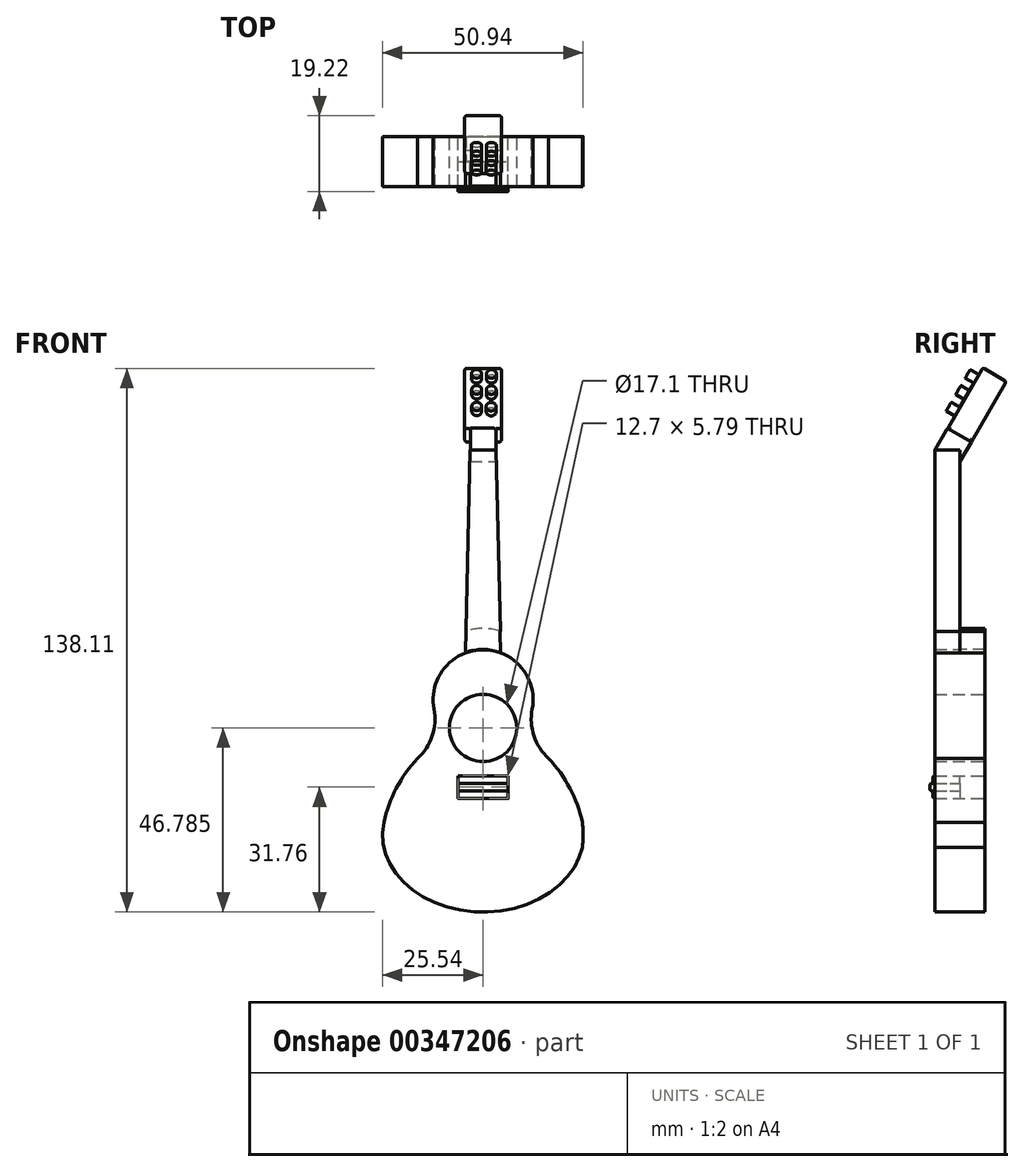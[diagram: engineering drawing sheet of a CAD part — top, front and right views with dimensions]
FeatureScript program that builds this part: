
annotation { "Feature Type Name" : "Feature", "Feature Type Description" : "" }
export const myFeature = defineFeature(function(context is Context, id is Id, definition is map)
    precondition{}
    {
        {
            var Q0;
            Q0=qCreatedBy(makeId("Front.planeOp"),FACE);
            var sketch = newSketch(context, id + "F0", { "sketchPlane" : qUnion([Q0])});
            skArc(sketch, "E0", {"start": v(12.47, 21.73) * mm, "mid": v(9.79, 32.21) * mm, "end": v(0, 36.82) * mm});
            skArc(sketch, "E1.trimOffspring", {"start": v(25.2, -13.37) * mm, "mid": v(25.4, -10.22) * mm, "end": v(25.2, -7.08) * mm});
            skPoint(sketch, "E2", {"position": v(16.65, 9.17) * mm});
            skArc(sketch, "E3", {"start": v(25.2, -7.08) * mm, "mid": v(22.06, 1.64) * mm, "end": v(16.65, 9.17) * mm});
            skPoint(sketch, "E4", {"position": v(12.47, 21.73) * mm});
            skArc(sketch, "E5", {"start": v(12.47, 21.73) * mm, "mid": v(12.93, 14.9) * mm, "end": v(16.65, 9.17) * mm});
            skEllipticalArc(sketch, "E6.trimOffspring", {});
            skArc(sketch, "E7.MirrorCS", {"start": v(-12.47, 21.73) * mm, "mid": v(-9.79, 32.21) * mm, "end": v(0, 36.82) * mm});
            skArc(sketch, "E8.MirrorCS", {"start": v(-12.47, 21.73) * mm, "mid": v(-12.93, 14.9) * mm, "end": v(-16.65, 9.17) * mm});
            skArc(sketch, "E9.MirrorCS", {"start": v(-25.2, -7.08) * mm, "mid": v(-22.06, 1.64) * mm, "end": v(-16.65, 9.17) * mm});
            skEllipticalArc(sketch, "E10.MirrorCS", {});
            skCircle(sketch, "E11", {"center": v(0, 16.96) * mm, "radius": 8.55 * mm});
            skLineSegment(sketch, "E12", {"start": v(-3.27, 87.62) * mm, "end": v(3.27, 87.62) * mm});
            skLineSegment(sketch, "E13", {"start": v(3.27, 87.62) * mm, "end": v(4.77, 24.05) * mm});
            skLineSegment(sketch, "E14.MirrorCS", {"start": v(-3.27, 87.62) * mm, "end": v(-4.77, 24.05) * mm});
            skPoint(sketch, "E15.end.orphan", {"position": v(0, 87.62) * mm});
            skArc(sketch, "E16.0", {"start": v(11.23, 21.97) * mm, "mid": v(8.8, 31.4) * mm, "end": v(0, 35.55) * mm});
            skArc(sketch, "E17.0", {"start": v(11.23, 21.97) * mm, "mid": v(11.72, 14.5) * mm, "end": v(15.8, 8.24) * mm});
            skArc(sketch, "E18.0", {"start": v(23.96, -7.34) * mm, "mid": v(20.93, 1.05) * mm, "end": v(15.73, 8.3) * mm});
            skFitSpline(sketch, "E19.0", {"points": [v(-24.19, -8.44) * mm, v(-24.3, -10.22) * mm, v(-24.19, -12) * mm, v(-23.85, -13.75) * mm, v(-23.29, -15.47) * mm, v(-22.5, -17.13) * mm, v(-21.52, -18.74) * mm, v(-20.32, -20.28) * mm, v(-19.15, -21.5) * mm, v(-18.12, -22.42) * mm, v(-17.29, -23.08) * mm, v(-16.42, -23.72) * mm, v(-15.21, -24.52) * mm, v(-13.6, -25.43) * mm, v(-11.56, -26.37) * mm, v(-9.4, -27.15) * mm, v(-7.15, -27.77) * mm, v(-4.82, -28.22) * mm, v(-2.83, -28.45) * mm, v(-1.22, -28.54) * mm, v(0, -28.57) * mm, v(1.22, -28.54) * mm, v(2.83, -28.45) * mm, v(4.82, -28.22) * mm, v(7.15, -27.77) * mm, v(9.4, -27.15) * mm, v(11.56, -26.37) * mm, v(13.6, -25.43) * mm, v(15.21, -24.52) * mm, v(16.42, -23.72) * mm, v(17.29, -23.08) * mm, v(18.12, -22.42) * mm, v(19.15, -21.5) * mm, v(20.32, -20.28) * mm, v(21.52, -18.74) * mm, v(22.5, -17.13) * mm, v(23.29, -15.47) * mm, v(23.85, -13.75) * mm, v(24.19, -12) * mm, v(24.3, -10.22) * mm, v(24.19, -8.44) * mm, v(23.85, -6.7) * mm, v(23.29, -4.98) * mm, v(22.5, -3.31) * mm, v(21.52, -1.7) * mm, v(20.32, -0.16) * mm, v(19.15, 1.05) * mm, v(18.12, 1.97) * mm, v(17.29, 2.64) * mm, v(16.42, 3.28) * mm, v(15.21, 4.07) * mm, v(13.6, 4.98) * mm, v(11.56, 5.93) * mm, v(9.4, 6.7) * mm, v(7.15, 7.33) * mm, v(4.82, 7.78) * mm, v(2.83, 8) * mm, v(1.22, 8.1) * mm, v(0, 8.12) * mm, v(-1.22, 8.1) * mm, v(-2.83, 8) * mm, v(-4.82, 7.78) * mm, v(-7.15, 7.33) * mm, v(-9.4, 6.7) * mm, v(-11.56, 5.93) * mm, v(-13.6, 4.98) * mm, v(-15.21, 4.07) * mm, v(-16.42, 3.28) * mm, v(-17.29, 2.64) * mm, v(-18.12, 1.97) * mm, v(-19.15, 1.05) * mm, v(-20.32, -0.16) * mm, v(-21.52, -1.7) * mm, v(-22.5, -3.31) * mm, v(-23.29, -4.98) * mm, v(-23.85, -6.7) * mm, v(-24.19, -8.44) * mm, v(-24.3, -10.22) * mm, v(-24.19, -12) * mm]});
            skArc(sketch, "E20.MirrorCS", {"start": v(-11.23, 21.97) * mm, "mid": v(-8.8, 31.4) * mm, "end": v(0, 35.55) * mm});
            skArc(sketch, "E21.MirrorCS", {"start": v(-23.96, -7.34) * mm, "mid": v(-20.93, 1.05) * mm, "end": v(-15.73, 8.3) * mm});
            skEllipticalArc(sketch, "E22.MirrorCS", {});
            skArc(sketch, "E23.0", {"start": v(-11.23, 21.97) * mm, "mid": v(-11.72, 14.5) * mm, "end": v(-15.8, 8.24) * mm});
            skFitSpline(sketch, "E24.0", {"points": [v(24.19, -12) * mm, v(24.3, -10.22) * mm, v(24.19, -8.44) * mm, v(23.85, -6.7) * mm, v(23.29, -4.98) * mm, v(22.5, -3.31) * mm, v(21.52, -1.7) * mm, v(20.32, -0.16) * mm, v(19.15, 1.05) * mm, v(18.12, 1.97) * mm, v(17.29, 2.64) * mm, v(16.42, 3.28) * mm, v(15.21, 4.07) * mm, v(13.6, 4.98) * mm, v(11.56, 5.93) * mm, v(9.4, 6.7) * mm, v(7.15, 7.33) * mm, v(4.82, 7.78) * mm, v(2.83, 8) * mm, v(1.22, 8.1) * mm, v(0, 8.12) * mm, v(-1.22, 8.1) * mm, v(-2.83, 8) * mm, v(-4.82, 7.78) * mm, v(-7.15, 7.33) * mm, v(-9.4, 6.7) * mm, v(-11.56, 5.93) * mm, v(-13.6, 4.98) * mm, v(-15.21, 4.07) * mm, v(-16.42, 3.28) * mm, v(-17.29, 2.64) * mm, v(-18.12, 1.97) * mm, v(-19.15, 1.05) * mm, v(-20.32, -0.16) * mm, v(-21.52, -1.7) * mm, v(-22.5, -3.31) * mm, v(-23.29, -4.98) * mm, v(-23.85, -6.7) * mm, v(-24.19, -8.44) * mm, v(-24.3, -10.22) * mm, v(-24.19, -12) * mm, v(-23.85, -13.75) * mm, v(-23.29, -15.47) * mm, v(-22.5, -17.13) * mm, v(-21.52, -18.74) * mm, v(-20.32, -20.28) * mm, v(-19.15, -21.5) * mm, v(-18.12, -22.42) * mm, v(-17.29, -23.08) * mm, v(-16.42, -23.72) * mm, v(-15.21, -24.52) * mm, v(-13.6, -25.43) * mm, v(-11.56, -26.37) * mm, v(-9.4, -27.15) * mm, v(-7.15, -27.77) * mm, v(-4.82, -28.22) * mm, v(-2.83, -28.45) * mm, v(-1.22, -28.54) * mm, v(0, -28.57) * mm, v(1.22, -28.54) * mm, v(2.83, -28.45) * mm, v(4.82, -28.22) * mm, v(7.15, -27.77) * mm, v(9.4, -27.15) * mm, v(11.56, -26.37) * mm, v(13.6, -25.43) * mm, v(15.21, -24.52) * mm, v(16.42, -23.72) * mm, v(17.29, -23.08) * mm, v(18.12, -22.42) * mm, v(19.15, -21.5) * mm, v(20.32, -20.28) * mm, v(21.52, -18.74) * mm, v(22.5, -17.13) * mm, v(23.29, -15.47) * mm, v(23.85, -13.75) * mm, v(24.19, -12) * mm, v(24.3, -10.22) * mm, v(24.19, -8.44) * mm]});
            skLineSegment(sketch, "E25.bottom", {"start": v(-6.35, 2.9) * mm, "end": v(6.35, 2.9) * mm});
            skLineSegment(sketch, "E25.top", {"start": v(-6.35, 4.83) * mm, "end": v(6.35, 4.83) * mm});
            skLineSegment(sketch, "E25.left", {"start": v(-6.35, 2.9) * mm, "end": v(-6.35, 4.83) * mm});
            skLineSegment(sketch, "E25.right", {"start": v(6.35, 2.9) * mm, "end": v(6.35, 4.83) * mm});
            skPoint(sketch, "E25.middle", {"position": v(0, 3.86) * mm});
            skLineSegment(sketch, "E26.top", {"start": v(-6.35, 0.97) * mm, "end": v(6.35, 0.97) * mm});
            skLineSegment(sketch, "E26.left", {"start": v(-6.35, 2.9) * mm, "end": v(-6.35, 0.97) * mm});
            skLineSegment(sketch, "E26.right", {"start": v(6.35, 2.9) * mm, "end": v(6.35, 0.97) * mm});
            skPoint(sketch, "E26.middle", {"position": v(0, 1.93) * mm});
            skLineSegment(sketch, "E27.top", {"start": v(-6.35, -0.97) * mm, "end": v(6.35, -0.97) * mm});
            skLineSegment(sketch, "E27.left", {"start": v(-6.35, 0.97) * mm, "end": v(-6.35, -0.97) * mm});
            skLineSegment(sketch, "E27.right", {"start": v(6.35, 0.97) * mm, "end": v(6.35, -0.97) * mm});
            skPoint(sketch, "E27.middle", {"position": v(0, 0) * mm});
            skLineSegment(sketch, "E28.MirrorCS", {"start": v(-4.36, 41.36) * mm, "end": v(-4.49, 36) * mm});
            skArc(sketch, "E29.1.0.0", {"start": v(4.49, 41.42) * mm, "mid": v(2.28, 42.03) * mm, "end": v(0, 42.23) * mm});
            skArc(sketch, "E29.1.0.1", {"start": v(-4.49, 41.42) * mm, "mid": v(-2.28, 42.03) * mm, "end": v(0, 42.23) * mm});
            skArc(sketch, "E29.1.0.2", {"start": v(-4.57, 36.07) * mm, "mid": v(-2.37, 36.68) * mm, "end": v(-0.09, 36.89) * mm});
            skLineSegment(sketch, "E29.1.0.3", {"start": v(-4.45, 41.43) * mm, "end": v(-4.57, 36.07) * mm});
            skArc(sketch, "E29.1.0.4", {"start": v(4.4, 36.07) * mm, "mid": v(2.2, 36.68) * mm, "end": v(-0.09, 36.89) * mm});
            skLineSegment(sketch, "E29.1.0.5", {"start": v(4.27, 41.5) * mm, "end": v(4.4, 36.07) * mm});
            const initialGuessF0  = {"E6.trimOffspring": [0, -0.010222538083282781, -1, 0, 0.025535106658935547, 0.019606885071617966, 1.5707963267948966, 3.302647404818477], "E10.MirrorCS": [0, -0.010222538083282781, 1, 0, 0.025535106658935547, 0.019606885071617966, 2.9805379023611094, 4.71238898038469], "E22.MirrorCS": [0, -0.010222538083282781, 1, 0, 0.025535106658935547, 0.019606885071617966, 2.9805379023611094, 4.71238898038469]};
            skSetInitialGuess(sketch, initialGuessF0);
            skSolve(sketch);
        }
        {
            var Q0;
            {var subQ8=sQuery(id+"F0.wireOp",EDGE,"E19.0");Q0=makeQuery(id+"F0.imprint","IMPRINT",FACE,{"disambiguationData":[TD([[makeQuery(id+"F0.imprint","IMPRINT",EDGE,{"derivedFrom":subQ8}),1.0]])]});}
            var Q1;
            {var subQ5=sQuery(id+"F0.wireOp",EDGE,"E1.trimOffspring");Q1=makeQuery(id+"F0.imprint","IMPRINT",FACE,{"disambiguationData":[TD([[makeQuery(id+"F0.imprint","IMPRINT",EDGE,{"derivedFrom":subQ5}),1.0]])]});}
            var Q2;
            {var subQ3=sQuery(id+"F0.wireOp",EDGE,"E13");var subQ5=sQuery(id+"F0.wireOp",EDGE,"E11");var subQ6=makeQuery(id+"F0.imprint","INTERSECT",VERTEX,{"derivedFrom":[subQ5,subQ3]});Q2=makeQuery(id+"F0.imprint","IMPRINT",FACE,{"disambiguationData":[TD([[makeQuery(id+"F0.imprint","IMPRINT",EDGE,{"disambiguationData":[TD([[subQ6,-1.0]])],"derivedFrom":subQ5}),-1.0]])]});}
            var Q3;
            {var subQ1=sQuery(id+"F0.wireOp",EDGE,"E7.MirrorCS");var subQ6=sQuery(id+"F0.wireOp",EDGE,"E0");var subQ10=makeQuery(id+"F0.imprint","INTERSECT",VERTEX,{"derivedFrom":[subQ6,subQ1]});Q3=makeQuery(id+"F0.imprint","IMPRINT",FACE,{"disambiguationData":[TD([[makeQuery(id+"F0.imprint","IMPRINT",EDGE,{"disambiguationData":[TD([[subQ10,1.0]])],"derivedFrom":subQ6}),1.0]])]});}
            extrude(context, id + "F1", {"entities" : qUnion([Q0, Q1, Q2, Q3]), "endBound" : BoundingType.SYMMETRIC, "depth" : 12.7 * mm});
        }
        {
            var Q0;
            {var subQ1=sQuery(id+"F0.wireOp",EDGE,"E12");Q0=makeQuery(id+"F0.imprint","IMPRINT",FACE,{"disambiguationData":[TD([[makeQuery(id+"F0.imprint","IMPRINT",EDGE,{"derivedFrom":subQ1}),-1.0]])]});}
            var Q1;
            {var subQ10=sQuery(id+"F0.wireOp",EDGE,"E29.1.0.4");Q1=makeQuery(id+"F0.imprint","IMPRINT",FACE,{"disambiguationData":[TD([[makeQuery(id+"F0.imprint","IMPRINT",EDGE,{"derivedFrom":subQ10}),-1.0]])]});}
            extrude(context, id + "F2", {"entities" : qUnion([Q0, Q1]), "operationType" : NewBodyOperationType.ADD, "depth" : 6.35 * mm});
        }
        {
            var Q0;
            {var subQ10=sQuery(id+"F0.wireOp",EDGE,"E29.1.0.4");Q0=makeQuery(id+"F0.imprint","IMPRINT",FACE,{"disambiguationData":[TD([[makeQuery(id+"F0.imprint","IMPRINT",EDGE,{"derivedFrom":subQ10}),-1.0]])]});}
            extrude(context, id + "F3", {"entities" : qUnion([Q0]), "oppositeDirection" : true, "depth" : 6.35 * mm});
        }
        {
            var Q0;
            Q0=makeQuery(id+"F0.imprint","IMPRINT",FACE,{"disambiguationData":[TD([[makeQuery(id+"F0.imprint","IMPRINT",EDGE,{"derivedFrom":sQuery(id+"F0.wireOp",EDGE,"E25.top")}),-1.0]])]});
            extrude(context, id + "F4", {"entities" : qUnion([Q0]), "depth" : 6.86 * mm});
        }
        {
            var Q0;
            Q0=makeQuery(id+"F0.imprint","IMPRINT",FACE,{"disambiguationData":[TD([[makeQuery(id+"F0.imprint","IMPRINT",EDGE,{"derivedFrom":sQuery(id+"F0.wireOp",EDGE,"E25.bottom")}),-1.0]])]});
            extrude(context, id + "F5", {"entities" : qUnion([Q0]), "depth" : 7.62 * mm});
        }
        {
            var Q0;
            Q0=makeQuery(id+"F0.imprint","IMPRINT",FACE,{"disambiguationData":[TD([[makeQuery(id+"F0.imprint","IMPRINT",EDGE,{"derivedFrom":sQuery(id+"F0.wireOp",EDGE,"E26.top")}),-1.0]])]});
            extrude(context, id + "F6", {"entities" : qUnion([Q0]), "depth" : 6.86 * mm});
        }
        {
            var Q0;
            Q0=makeQuery(id+"F4.opExtrude","CAP_EDGE",EDGE,{"disambiguationData":[OSD([sQuery(id+"F0.wireOp",EDGE,"E25.top")])],"isStart":false});
            var Q1;
            Q1=makeQuery(id+"F4.opExtrude","CAP_EDGE",EDGE,{"disambiguationData":[OSD([sQuery(id+"F0.wireOp",EDGE,"E25.bottom")])],"isStart":false});
            var Q2;
            Q2=makeQuery(id+"F5.opExtrude","CAP_EDGE",EDGE,{"disambiguationData":[OSD([sQuery(id+"F0.wireOp",EDGE,"E25.bottom")])],"isStart":false});
            var Q3;
            Q3=makeQuery(id+"F5.opExtrude","CAP_EDGE",EDGE,{"disambiguationData":[OSD([sQuery(id+"F0.wireOp",EDGE,"E26.top")])],"isStart":false});
            var Q4;
            Q4=makeQuery(id+"F6.opExtrude","CAP_EDGE",EDGE,{"disambiguationData":[OSD([sQuery(id+"F0.wireOp",EDGE,"E26.top")])],"isStart":false});
            var Q5;
            Q5=makeQuery(id+"F6.opExtrude","CAP_EDGE",EDGE,{"disambiguationData":[OSD([sQuery(id+"F0.wireOp",EDGE,"E27.top")])],"isStart":false});
            fillet(context, id + "F7", {"entities" : qUnion([Q0, Q1, Q2, Q3, Q4, Q5]), "radius" : 0.5 * mm, "tangentPropagation" : true, "allowEdgeOverflow" : false});
        }
        {
            var Q0;
            Q0=makeQuery(id+"F2.opExtrude","CAP_EDGE",EDGE,{"disambiguationData":[OSD([sQuery(id+"F0.wireOp",EDGE,"E12")])],"isStart":false});
            cPlane(context, id + "F8", {"entities" : qUnion([Q0]), "cplaneType" : CPlaneType.LINE_ANGLE, "offset" : 25.4 * mm, "angle" : 60 * degree, "width" : 152.4 * mm, "height" : 152.4 * mm});
        }
        {
            var Q0;
            Q0=qCreatedBy(id+"F8.planeOp",FACE);
            var sketch = newSketch(context, id + "F9", { "sketchPlane" : qUnion([Q0])});
            skLineSegment(sketch, "E30.top", {"start": v(-3.26, -49.27) * mm, "end": v(3.23, -49.27) * mm});
            skLineSegment(sketch, "E30.left", {"start": v(-3.26, -42.3) * mm, "end": v(-3.26, -49.27) * mm});
            skLineSegment(sketch, "E30.right", {"start": v(3.23, -42.3) * mm, "end": v(3.23, -49.27) * mm});
            skLineSegment(sketch, "E31.bottom", {"start": v(-3.26, -42.3) * mm, "end": v(3.26, -42.3) * mm});
            skSolve(sketch);
        }
        {
            var Q0;
            Q0 = qSketchRegion(id + "F9", true);
            extrude(context, id + "F10", {"entities" : qUnion([Q0]), "operationType" : NewBodyOperationType.ADD, "depth" : 6.35 * mm});
        }
        {
            var Q0;
            Q0=makeQuery(id+"F10.opExtrude","CAP_FACE",FACE,{"disambiguationData":[OSD([sQuery(id+"F9.wireOp",EDGE,"E30.top"),sQuery(id+"F9.wireOp",EDGE,"E30.left"),sQuery(id+"F9.wireOp",EDGE,"E30.right"),sQuery(id+"F9.wireOp",EDGE,"E31.bottom")])],"isStart":false});
            var sketch = newSketch(context, id + "F11", { "sketchPlane" : qUnion([Q0])});
            skLineSegment(sketch, "E32.bottom", {"start": v(-4.67, -49.21) * mm, "end": v(4.67, -49.21) * mm});
            skLineSegment(sketch, "E32.top", {"start": v(-4.67, -42.3) * mm, "end": v(4.67, -42.3) * mm});
            skLineSegment(sketch, "E32.left", {"start": v(-4.67, -49.21) * mm, "end": v(-4.67, -42.3) * mm});
            skLineSegment(sketch, "E32.right", {"start": v(4.67, -49.21) * mm, "end": v(4.67, -42.3) * mm});
            skPoint(sketch, "E32.middle", {"position": v(0, -45.76) * mm});
            skSolve(sketch);
        }
        {
            var Q0;
            {var subQ5=makeQuery(id+"F10.opExtrude","CAP_EDGE",EDGE,{"disambiguationData":[OSD([sQuery(id+"F9.wireOp",EDGE,"E31.bottom")])],"isStart":false});Q0=makeQuery(id+"F11.imprint","IMPRINT",FACE,{"disambiguationData":[TD([[makeQuery(id+"F11.imprint","IMPRINT",EDGE,{"derivedFrom":subQ5}),-1.0]])]});}
            var Q1;
            Q1=makeQuery(id+"F11.imprint","IMPRINT",FACE,{"disambiguationData":[TD([[makeQuery(id+"F11.imprint","IMPRINT",EDGE,{"derivedFrom":sQuery(id+"F11.wireOp",EDGE,"E32.top")}),-1.0]])]});
            extrude(context, id + "F12", {"entities" : qUnion([Q0, Q1]), "operationType" : NewBodyOperationType.ADD, "depth" : 17.78 * mm});
        }
        {
            var Q0;
            Q0=makeQuery(id+"F12.opExtrude","SWEPT_EDGE",EDGE,{"disambiguationData":[OSD([sQuery(id+"F11.wireOp",EDGE,"E32.bottom"),sQuery(id+"F11.wireOp",EDGE,"E32.left")])]});
            var Q1;
            Q1=makeQuery(id+"F12.opExtrude","SWEPT_EDGE",EDGE,{"disambiguationData":[OSD([sQuery(id+"F11.wireOp",EDGE,"E32.bottom"),sQuery(id+"F11.wireOp",EDGE,"E32.right")])]});
            var Q2;
            Q2=makeQuery(id+"F12.opExtrude","SWEPT_EDGE",EDGE,{"disambiguationData":[OSD([sQuery(id+"F11.wireOp",EDGE,"E32.top"),sQuery(id+"F11.wireOp",EDGE,"E32.right")])]});
            var Q3;
            Q3=makeQuery(id+"F12.opExtrude","SWEPT_EDGE",EDGE,{"disambiguationData":[OSD([sQuery(id+"F11.wireOp",EDGE,"E32.top"),sQuery(id+"F11.wireOp",EDGE,"E32.left")])]});
            var Q4;
            Q4=makeQuery(id+"F12.opExtrude","CAP_EDGE",EDGE,{"disambiguationData":[OSD([sQuery(id+"F11.wireOp",EDGE,"E32.left")])],"isStart":false});
            var Q5;
            Q5=makeQuery(id+"F12.opExtrude","CAP_EDGE",EDGE,{"disambiguationData":[OSD([sQuery(id+"F11.wireOp",EDGE,"E32.left")])],"isStart":true});
            var Q6;
            Q6=makeQuery(id+"F12.opExtrude","CAP_EDGE",EDGE,{"disambiguationData":[OSD([sQuery(id+"F11.wireOp",EDGE,"E32.right")])],"isStart":true});
            var Q7;
            Q7=makeQuery(id+"F12.opExtrude","CAP_EDGE",EDGE,{"disambiguationData":[OSD([sQuery(id+"F11.wireOp",EDGE,"E32.top")])],"isStart":false});
            var Q8;
            Q8=makeQuery(id+"F12.opExtrude","CAP_EDGE",EDGE,{"disambiguationData":[OSD([sQuery(id+"F11.wireOp",EDGE,"E32.bottom")])],"isStart":false});
            var Q9;
            Q9=makeQuery(id+"F12.opExtrude","CAP_EDGE",EDGE,{"disambiguationData":[OSD([sQuery(id+"F11.wireOp",EDGE,"E32.right")])],"isStart":false});
            fillet(context, id + "F13", {"entities" : qUnion([Q0, Q1, Q2, Q3, Q4, Q5, Q6, Q7, Q8, Q9]), "radius" : 0.5 * mm, "tangentPropagation" : true, "allowEdgeOverflow" : false});
        }
        {
            var Q0;
            {var subQ0=sQuery(id+"F9.wireOp",EDGE,"E30.left");Q0=makeQuery(id+"F12.boolean.opBoolean","SPLIT",EDGE,{"disambiguationData":[topologyDisambiguationEdgeConnected([makeQuery(id+"F12.opExtrude","CAP_FACE",FACE,{"disambiguationData":[OSD([sQuery(id+"F11.wireOp",EDGE,"E32.bottom"),sQuery(id+"F11.wireOp",EDGE,"E32.top"),sQuery(id+"F11.wireOp",EDGE,"E32.left"),sQuery(id+"F11.wireOp",EDGE,"E32.right")])],"isStart":true})])],"derivedFrom":makeQuery(id+"F10.opExtrude","CAP_EDGE",EDGE,{"disambiguationData":[OSD([subQ0])],"isStart":false})});}
            var Q1;
            {var subQ0=sQuery(id+"F9.wireOp",EDGE,"E30.right");Q1=makeQuery(id+"F12.boolean.opBoolean","SPLIT",EDGE,{"disambiguationData":[topologyDisambiguationEdgeConnected([makeQuery(id+"F12.opExtrude","CAP_FACE",FACE,{"disambiguationData":[OSD([sQuery(id+"F11.wireOp",EDGE,"E32.bottom"),sQuery(id+"F11.wireOp",EDGE,"E32.top"),sQuery(id+"F11.wireOp",EDGE,"E32.left"),sQuery(id+"F11.wireOp",EDGE,"E32.right")])],"isStart":true})])],"derivedFrom":makeQuery(id+"F10.opExtrude","CAP_EDGE",EDGE,{"disambiguationData":[OSD([subQ0])],"isStart":false})});}
            fillet(context, id + "F14", {"entities" : qUnion([Q0, Q1]), "radius" : 0.5 * mm, "tangentPropagation" : true, "allowEdgeOverflow" : false});
        }
        {
            var Q0;
            Q0=makeQuery(id+"F12.opExtrude","SWEPT_FACE",FACE,{"disambiguationData":[OSD([sQuery(id+"F11.wireOp",EDGE,"E32.bottom")])]});
            var sketch = newSketch(context, id + "F15", { "sketchPlane" : qUnion([Q0])});
            skCircle(sketch, "E33", {"center": v(-1.66, 93.6) * mm, "radius": 1.26 * mm});
            skCircle(sketch, "E34", {"center": v(-1.62, 88.91) * mm, "radius": 1.26 * mm});
            skCircle(sketch, "E35", {"center": v(-1.63, 84.02) * mm, "radius": 1.25 * mm});
            skCircle(sketch, "E36", {"center": v(2.13, 93.55) * mm, "radius": 1.26 * mm});
            skCircle(sketch, "E37", {"center": v(2.08, 88.83) * mm, "radius": 1.26 * mm});
            skCircle(sketch, "E38", {"center": v(2.04, 83.96) * mm, "radius": 1.26 * mm});
            skSolve(sketch);
        }
        {
            var Q0;
            Q0=makeQuery(id+"F15.imprint","IMPRINT",FACE,{"disambiguationData":[TD([[makeQuery(id+"F15.imprint","IMPRINT",EDGE,{"derivedFrom":sQuery(id+"F15.wireOp",EDGE,"E33")}),1.0]])]});
            var Q1;
            Q1=makeQuery(id+"F15.imprint","IMPRINT",FACE,{"disambiguationData":[TD([[makeQuery(id+"F15.imprint","IMPRINT",EDGE,{"derivedFrom":sQuery(id+"F15.wireOp",EDGE,"E36")}),1.0]])]});
            var Q2;
            Q2=makeQuery(id+"F15.imprint","IMPRINT",FACE,{"disambiguationData":[TD([[makeQuery(id+"F15.imprint","IMPRINT",EDGE,{"derivedFrom":sQuery(id+"F15.wireOp",EDGE,"E37")}),1.0]])]});
            var Q3;
            Q3=makeQuery(id+"F15.imprint","IMPRINT",FACE,{"disambiguationData":[TD([[makeQuery(id+"F15.imprint","IMPRINT",EDGE,{"derivedFrom":sQuery(id+"F15.wireOp",EDGE,"E34")}),1.0]])]});
            var Q4;
            Q4=makeQuery(id+"F15.imprint","IMPRINT",FACE,{"disambiguationData":[TD([[makeQuery(id+"F15.imprint","IMPRINT",EDGE,{"derivedFrom":sQuery(id+"F15.wireOp",EDGE,"E35")}),1.0]])]});
            var Q5;
            Q5=makeQuery(id+"F15.imprint","IMPRINT",FACE,{"disambiguationData":[TD([[makeQuery(id+"F15.imprint","IMPRINT",EDGE,{"derivedFrom":sQuery(id+"F15.wireOp",EDGE,"E38")}),1.0]])]});
            extrude(context, id + "F16", {"entities" : qUnion([Q0, Q1, Q2, Q3, Q4, Q5]), "operationType" : NewBodyOperationType.ADD, "depth" : 2.54 * mm});
        }
        {
            var Q0;
            Q0=makeQuery(id+"F2.opExtrude","CAP_FACE",FACE,{"disambiguationData":[OSD([sQuery(id+"F0.wireOp",EDGE,"E12"),sQuery(id+"F0.wireOp",EDGE,"E13"),sQuery(id+"F0.wireOp",EDGE,"E14.MirrorCS"),sQuery(id+"F0.wireOp",EDGE,"E28.MirrorCS"),sQuery(id+"F0.wireOp",EDGE,"E29.1.0.0"),sQuery(id+"F0.wireOp",EDGE,"E29.1.0.2"),sQuery(id+"F0.wireOp",EDGE,"E29.1.0.4"),sQuery(id+"F0.wireOp",EDGE,"E29.1.0.5")])],"isStart":false});
            var sketch = newSketch(context, id + "F17", { "sketchPlane" : qUnion([Q0])});
            skLineSegment(sketch, "E39.bottom", {"start": v(-3.27, 87.62) * mm, "end": v(3.27, 87.62) * mm});
            skLineSegment(sketch, "E39.top", {"start": v(-3.35, 84) * mm, "end": v(3.35, 84) * mm});
            skLineSegment(sketch, "E40.top", {"start": v(-3.44, 80.36) * mm, "end": v(3.43, 80.36) * mm});
            skLineSegment(sketch, "E41.top", {"start": v(6.81, 76.71) * mm, "end": v(6.85, 76.71) * mm});
            skLineSegment(sketch, "E41.left", {"start": v(-6.05, 76.72) * mm, "end": v(-6.05, 76.71) * mm});
            skLineSegment(sketch, "E42.bottom", {"start": v(-6.08, 76.72) * mm, "end": v(-6.05, 76.72) * mm});
            skLineSegment(sketch, "E42.top", {"start": v(-3.61, 73.1) * mm, "end": v(3.59, 73.1) * mm});
            skLineSegment(sketch, "E42.right", {"start": v(6.81, 76.72) * mm, "end": v(6.81, 76.71) * mm});
            skLineSegment(sketch, "E43.top", {"start": v(-3.7, 69.46) * mm, "end": v(3.67, 69.46) * mm});
            skLineSegment(sketch, "E44.right", {"start": v(6.9, 65.84) * mm, "end": v(6.9, 65.82) * mm});
            skLineSegment(sketch, "E45.bottom", {"start": v(6.9, 65.84) * mm, "end": v(7, 65.84) * mm});
            skLineSegment(sketch, "E45.left", {"start": v(-5.9, 65.84) * mm, "end": v(-5.9, 65.82) * mm});
            skLineSegment(sketch, "E46.bottom", {"start": v(-3.87, 62.2) * mm, "end": v(3.83, 62.2) * mm});
            skLineSegment(sketch, "E46.top", {"start": v(-3.95, 58.57) * mm, "end": v(3.9, 58.57) * mm});
            skLineSegment(sketch, "E47.top", {"start": v(-4.04, 54.89) * mm, "end": v(3.99, 54.89) * mm});
            skLineSegment(sketch, "E48.top", {"start": v(-4.13, 51.26) * mm, "end": v(4.07, 51.26) * mm});
            skLineSegment(sketch, "E49.bottom", {"start": v(-4.13, 51.23) * mm, "end": v(4.07, 51.23) * mm});
            skLineSegment(sketch, "E49.top", {"start": v(7.15, 47.6) * mm, "end": v(7.19, 47.6) * mm});
            skLineSegment(sketch, "E49.left", {"start": v(-5.7, 47.62) * mm, "end": v(-5.7, 47.6) * mm});
            skLineSegment(sketch, "E50.right", {"start": v(7.15, 47.62) * mm, "end": v(7.15, 47.6) * mm});
            skLineSegment(sketch, "E51.bottom", {"start": v(-4.3, 44) * mm, "end": v(4.23, 44) * mm});
            skLineSegment(sketch, "E52.bottom", {"start": v(-4.39, 40.3) * mm, "end": v(4.3, 40.3) * mm});
            skLineSegment(sketch, "E53.bottom", {"start": v(-5.84, 36.69) * mm, "end": v(-5.8, 36.69) * mm});
            skLineSegment(sketch, "E53.right", {"start": v(7.05, 36.69) * mm, "end": v(7.05, 36.67) * mm});
            skLineSegment(sketch, "E54", {"start": v(-3.78, 65.82) * mm, "end": v(3.75, 65.82) * mm});
            skLineSegment(sketch, "E55", {"start": v(-3.53, 76.71) * mm, "end": v(3.5, 76.71) * mm});
            skPoint(sketch, "E56.orphan", {"position": v(-6.05, 87.62) * mm});
            skLineSegment(sketch, "E57.trimOffspring", {"start": v(-4.21, 47.62) * mm, "end": v(4.15, 47.62) * mm});
            skSolve(sketch);
        }
        {
            var Q0;
            Q0=sQuery(id+"F17.wireOp",EDGE,"E39.top");
            var Q1;
            Q1=sQuery(id+"F17.wireOp",EDGE,"E40.top");
            var Q2;
            Q2=sQuery(id+"F17.wireOp",EDGE,"E55");
            var Q3;
            Q3=sQuery(id+"F17.wireOp",EDGE,"E42.top");
            var Q4;
            Q4=sQuery(id+"F17.wireOp",EDGE,"E43.top");
            var Q5;
            Q5=sQuery(id+"F17.wireOp",EDGE,"E54");
            extrude(context, id + "F18", {"bodyType" : ToolBodyType.SURFACE, "surfaceEntities" : qUnion([Q0, Q1, Q2, Q3, Q4, Q5]), "depth" : 0.5 * mm});
        }
        {
            var Q0;
            Q0=sQuery(id+"F17.wireOp",EDGE,"E46.bottom");
            var Q1;
            Q1=sQuery(id+"F17.wireOp",EDGE,"E46.top");
            var Q2;
            Q2=sQuery(id+"F17.wireOp",EDGE,"E47.top");
            var Q3;
            Q3=sQuery(id+"F17.wireOp",EDGE,"E49.bottom");
            var Q4;
            Q4=sQuery(id+"F17.wireOp",EDGE,"E57.trimOffspring");
            var Q5;
            Q5=sQuery(id+"F17.wireOp",EDGE,"E51.bottom");
            var Q6;
            Q6=sQuery(id+"F17.wireOp",EDGE,"E52.bottom");
            extrude(context, id + "F19", {"bodyType" : ToolBodyType.SURFACE, "surfaceEntities" : qUnion([Q0, Q1, Q2, Q3, Q4, Q5, Q6]), "depth" : 0.5 * mm});
        }
        {
            var Q0;
            Q0=makeQuery(id+"F2.opExtrude","CAP_FACE",FACE,{"disambiguationData":[OSD([sQuery(id+"F0.wireOp",EDGE,"E12"),sQuery(id+"F0.wireOp",EDGE,"E13"),sQuery(id+"F0.wireOp",EDGE,"E14.MirrorCS"),sQuery(id+"F0.wireOp",EDGE,"E28.MirrorCS"),sQuery(id+"F0.wireOp",EDGE,"E29.1.0.0"),sQuery(id+"F0.wireOp",EDGE,"E29.1.0.2"),sQuery(id+"F0.wireOp",EDGE,"E29.1.0.4"),sQuery(id+"F0.wireOp",EDGE,"E29.1.0.5")])],"isStart":false});
            var sketch = newSketch(context, id + "F20", { "sketchPlane" : qUnion([Q0])});
            skCircle(sketch, "E58", {"center": v(0, 56.7) * mm, "radius": 0.89 * mm});
            skCircle(sketch, "E59", {"center": v(-2.06, 49.55) * mm, "radius": 0.89 * mm});
            skCircle(sketch, "E60", {"center": v(2.08, 49.47) * mm, "radius": 0.89 * mm});
            skCircle(sketch, "E61", {"center": v(0, 42.25) * mm, "radius": 0.89 * mm});
            skSolve(sketch);
        }
        {
            var Q0;
            Q0=sQuery(id+"F20.wireOp",EDGE,"E58");
            var Q1;
            Q1=sQuery(id+"F20.wireOp",EDGE,"E60");
            var Q2;
            Q2=sQuery(id+"F20.wireOp",EDGE,"E61");
            var Q3;
            Q3=sQuery(id+"F20.wireOp",EDGE,"E59");
            extrude(context, id + "F21", {"bodyType" : ToolBodyType.SURFACE, "surfaceEntities" : qUnion([Q0, Q1, Q2, Q3]), "depth" : 0.25 * mm});
        }
        {
            var Q0;
            Q0=makeQuery(id+"F12.opExtrude","SWEPT_FACE",FACE,{"disambiguationData":[OSD([sQuery(id+"F11.wireOp",EDGE,"E32.bottom")])]});
            var sketch = newSketch(context, id + "F22", { "sketchPlane" : qUnion([Q0])});
            skLineSegment(sketch, "E62", {"start": v(-0.38, 84.05) * mm, "end": v(-0.38, 79.05) * mm});
            skLineSegment(sketch, "E63", {"start": v(0.8, 84.09) * mm, "end": v(0.8, 79.05) * mm});
            skLineSegment(sketch, "E64", {"start": v(0.48, 79.05) * mm, "end": v(0.48, 88.3) * mm});
            skArc(sketch, "E65", {"start": v(-0.38, 79.05) * mm, "mid": v(-1.14, 75.58) * mm, "end": v(-3.28, 72.75) * mm});
            skArc(sketch, "E66", {"start": v(0.8, 79.05) * mm, "mid": v(1.42, 75.67) * mm, "end": v(3.22, 72.74) * mm});
            skArc(sketch, "E67", {"start": v(0, 79.05) * mm, "mid": v(-0.44, 75.78) * mm, "end": v(-1.73, 72.74) * mm});
            skArc(sketch, "E68", {"start": v(0.48, 79.05) * mm, "mid": v(0.88, 75.78) * mm, "end": v(2.07, 72.7) * mm});
            skLineSegment(sketch, "E69", {"start": v(0, 88.3) * mm, "end": v(0, 79.05) * mm});
            skArc(sketch, "E70", {"start": v(0, 88.3) * mm, "mid": v(-0.13, 88.95) * mm, "end": v(-0.5, 89.51) * mm});
            skArc(sketch, "E71", {"start": v(0.48, 88.3) * mm, "mid": v(0.63, 89) * mm, "end": v(1.05, 89.56) * mm});
            skLineSegment(sketch, "E72", {"start": v(0.34, 79.05) * mm, "end": v(0.34, 93.45) * mm});
            skLineSegment(sketch, "E73", {"start": v(0.14, 79.05) * mm, "end": v(0.14, 93.45) * mm});
            skArc(sketch, "E74", {"start": v(0.14, 93.45) * mm, "mid": v(-0.16, 94.22) * mm, "end": v(-0.9, 94.6) * mm});
            skArc(sketch, "E75", {"start": v(0.34, 93.45) * mm, "mid": v(0.66, 94.25) * mm, "end": v(1.44, 94.6) * mm});
            skArc(sketch, "E76", {"start": v(0.34, 79.05) * mm, "mid": v(0.42, 75.92) * mm, "end": v(0.66, 72.8) * mm});
            skArc(sketch, "E77", {"start": v(0.14, 79.05) * mm, "mid": v(0.06, 75.92) * mm, "end": v(-0.17, 72.79) * mm});
            skSolve(sketch);
        }
        {
            var Q0;
            Q0=sQuery(id+"F22.wireOp",EDGE,"E70");
            var Q1;
            Q1=sQuery(id+"F22.wireOp",EDGE,"E73");
            var Q2;
            Q2=sQuery(id+"F22.wireOp",EDGE,"E72");
            var Q3;
            Q3=sQuery(id+"F22.wireOp",EDGE,"E64");
            var Q4;
            Q4=sQuery(id+"F22.wireOp",EDGE,"E71");
            var Q5;
            Q5=sQuery(id+"F22.wireOp",EDGE,"E69");
            var Q6;
            Q6=sQuery(id+"F22.wireOp",EDGE,"E75");
            var Q7;
            Q7=sQuery(id+"F22.wireOp",EDGE,"E74");
            var Q8;
            Q8=sQuery(id+"F22.wireOp",EDGE,"E62");
            var Q9;
            Q9=sQuery(id+"F22.wireOp",EDGE,"E63");
            extrude(context, id + "F23", {"bodyType" : ToolBodyType.SURFACE, "surfaceEntities" : qUnion([Q0, Q1, Q2, Q3, Q4, Q5, Q6, Q7, Q8, Q9]), "depth" : 0.25 * mm});
        }
        {
            var Q0;
            Q0=sQuery(id+"F22.wireOp",EDGE,"E65");
            var Q1;
            Q1=sQuery(id+"F22.wireOp",EDGE,"E66");
            var Q2;
            Q2=sQuery(id+"F22.wireOp",EDGE,"E68");
            var Q3;
            Q3=sQuery(id+"F22.wireOp",EDGE,"E76");
            var Q4;
            Q4=sQuery(id+"F22.wireOp",EDGE,"E77");
            var Q5;
            Q5=sQuery(id+"F22.wireOp",EDGE,"E67");
            extrude(context, id + "F24", {"bodyType" : ToolBodyType.SURFACE, "surfaceEntities" : qUnion([Q0, Q1, Q2, Q3, Q4, Q5]), "depth" : 0.25 * mm});
        }
        {
            var Q0;
            Q0=makeQuery(id+"F2.opExtrude","CAP_FACE",FACE,{"disambiguationData":[OSD([sQuery(id+"F0.wireOp",EDGE,"E12"),sQuery(id+"F0.wireOp",EDGE,"E13"),sQuery(id+"F0.wireOp",EDGE,"E14.MirrorCS"),sQuery(id+"F0.wireOp",EDGE,"E28.MirrorCS"),sQuery(id+"F0.wireOp",EDGE,"E29.1.0.0"),sQuery(id+"F0.wireOp",EDGE,"E29.1.0.2"),sQuery(id+"F0.wireOp",EDGE,"E29.1.0.4"),sQuery(id+"F0.wireOp",EDGE,"E29.1.0.5")])],"isStart":false});
            var sketch = newSketch(context, id + "F25", { "sketchPlane" : qUnion([Q0])});
            skLineSegment(sketch, "E78", {"start": v(-3.27, 87.62) * mm, "end": v(-4.48, 36.1) * mm});
            skLineSegment(sketch, "E79", {"start": v(-1.75, 87.62) * mm, "end": v(-2.72, 36.61) * mm});
            skLineSegment(sketch, "E80", {"start": v(0, 87.62) * mm, "end": v(-0.82, 36.87) * mm});
            skLineSegment(sketch, "E81", {"start": v(2.06, 87.62) * mm, "end": v(2.06, 36.7) * mm});
            skLineSegment(sketch, "E82", {"start": v(3.27, 87.62) * mm, "end": v(4.4, 36.07) * mm});
            skLineSegment(sketch, "E83", {"start": v(0.65, 87.62) * mm, "end": v(-0.17, 36.87) * mm});
            skSolve(sketch);
        }
        {
            var Q0;
            Q0=sQuery(id+"F25.wireOp",EDGE,"E78");
            var Q1;
            Q1=sQuery(id+"F25.wireOp",EDGE,"E79");
            var Q2;
            Q2=sQuery(id+"F25.wireOp",EDGE,"E80");
            var Q3;
            Q3=sQuery(id+"F25.wireOp",EDGE,"E83");
            var Q4;
            Q4=sQuery(id+"F25.wireOp",EDGE,"E81");
            var Q5;
            Q5=sQuery(id+"F25.wireOp",EDGE,"E82");
            extrude(context, id + "F26", {"bodyType" : ToolBodyType.SURFACE, "surfaceEntities" : qUnion([Q0, Q1, Q2, Q3, Q4, Q5]), "depth" : 0.25 * mm});
        }
        {
            var Q0;
            Q0=makeQuery(id+"F1.opExtrude","CAP_FACE",FACE,{"disambiguationData":[OSD([sQuery(id+"F0.wireOp",EDGE,"E0"),sQuery(id+"F0.wireOp",EDGE,"E1.trimOffspring"),sQuery(id+"F0.wireOp",EDGE,"E3"),sQuery(id+"F0.wireOp",EDGE,"E5"),sQuery(id+"F0.wireOp",EDGE,"E6.trimOffspring"),sQuery(id+"F0.wireOp",EDGE,"E7.MirrorCS"),sQuery(id+"F0.wireOp",EDGE,"E8.MirrorCS"),sQuery(id+"F0.wireOp",EDGE,"E9.MirrorCS"),sQuery(id+"F0.wireOp",EDGE,"E11"),sQuery(id+"F0.wireOp",EDGE,"E22.MirrorCS"),sQuery(id+"F0.wireOp",EDGE,"E25.top"),sQuery(id+"F0.wireOp",EDGE,"E25.left"),sQuery(id+"F0.wireOp",EDGE,"E25.right"),sQuery(id+"F0.wireOp",EDGE,"E26.left"),sQuery(id+"F0.wireOp",EDGE,"E26.right"),sQuery(id+"F0.wireOp",EDGE,"E27.top"),sQuery(id+"F0.wireOp",EDGE,"E27.left"),sQuery(id+"F0.wireOp",EDGE,"E27.right")])],"isStart":false});
            var sketch = newSketch(context, id + "F27", { "sketchPlane" : qUnion([Q0])});
            skLineSegment(sketch, "E84", {"start": v(-4.56, 35.97) * mm, "end": v(-4.56, 9.72) * mm});
            skLineSegment(sketch, "E85", {"start": v(-2.66, 36.54) * mm, "end": v(-2.66, 8.83) * mm});
            skLineSegment(sketch, "E86", {"start": v(-0.85, 36.79) * mm, "end": v(-0.85, 8.45) * mm});
            skLineSegment(sketch, "E87", {"start": v(0, 36.82) * mm, "end": v(0, 8.4) * mm});
            skPoint(sketch, "E87.endSnap0", {"position": v(0, 9.38) * mm});
            skLineSegment(sketch, "E88", {"start": v(2.05, 36.65) * mm, "end": v(2.05, 8.65) * mm});
            skLineSegment(sketch, "E89", {"start": v(4.6, 35.95) * mm, "end": v(4.6, 9.75) * mm});
            skSolve(sketch);
        }
        {
            var Q0;
            Q0=sQuery(id+"F27.wireOp",EDGE,"E87");
            var Q1;
            Q1=sQuery(id+"F27.wireOp",EDGE,"E88");
            var Q2;
            Q2=sQuery(id+"F27.wireOp",EDGE,"E89");
            var Q3;
            Q3=sQuery(id+"F27.wireOp",EDGE,"E86");
            var Q4;
            Q4=sQuery(id+"F27.wireOp",EDGE,"E85");
            var Q5;
            Q5=sQuery(id+"F27.wireOp",EDGE,"E84");
            extrude(context, id + "F28", {"bodyType" : ToolBodyType.SURFACE, "surfaceEntities" : qUnion([Q0, Q1, Q2, Q3, Q4, Q5]), "depth" : 0.25 * mm});
        }
    });
